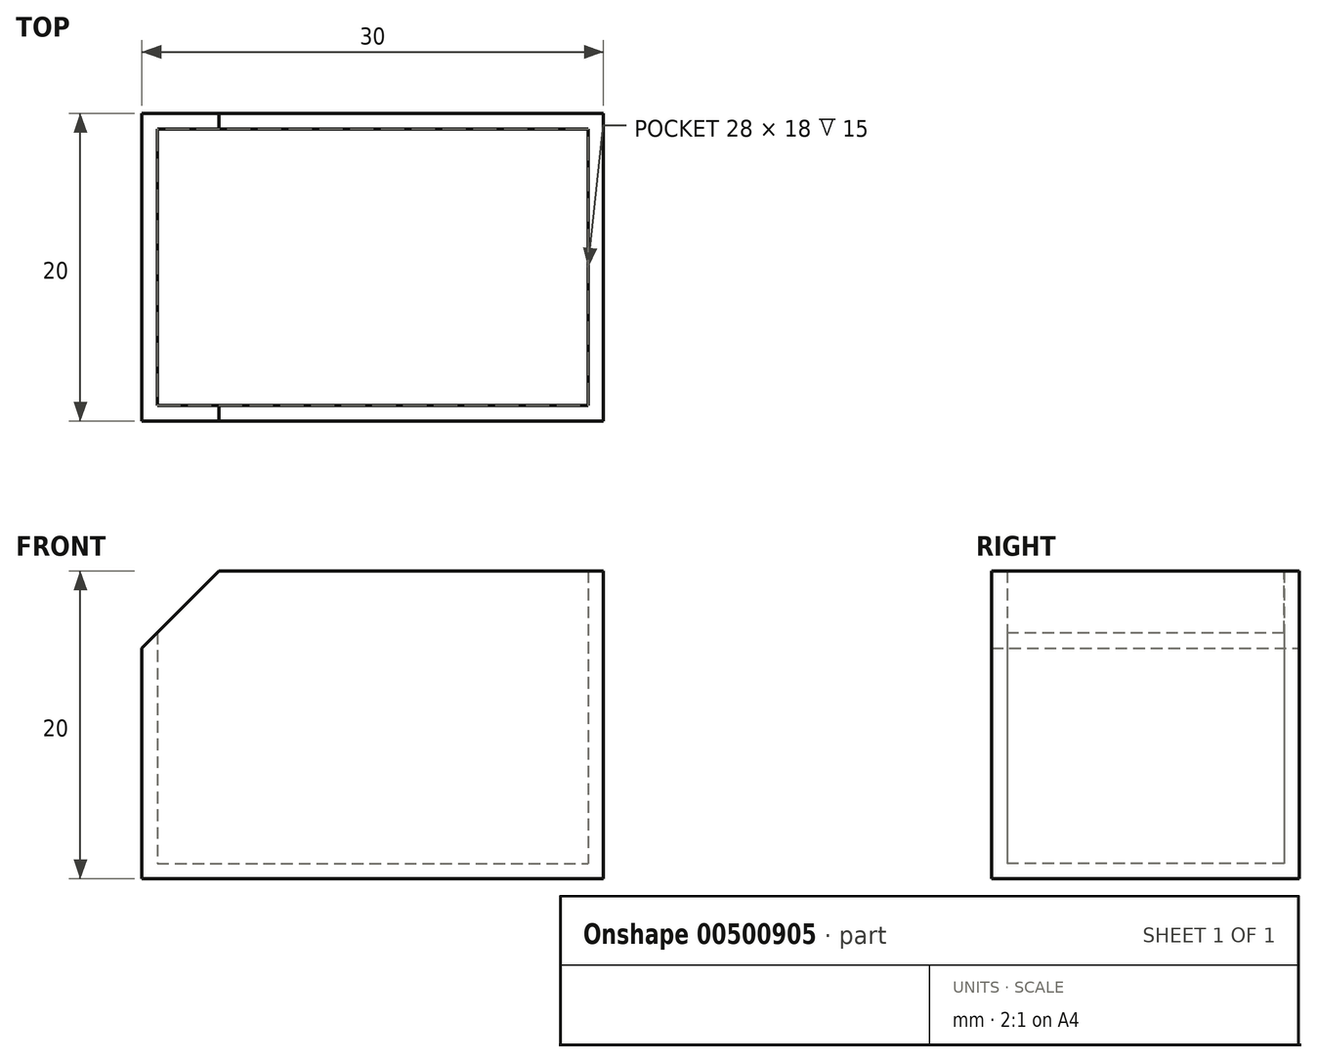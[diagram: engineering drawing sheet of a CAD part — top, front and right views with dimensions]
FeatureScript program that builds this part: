
annotation { "Feature Type Name" : "Feature", "Feature Type Description" : "" }
export const myFeature = defineFeature(function(context is Context, id is Id, definition is map)
    precondition{}
    {
        {
            var Q0;
            Q0=qCreatedBy(makeId("Front.planeOp"),FACE);
            var sketch = newSketch(context, id + "F0", { "sketchPlane" : qUnion([Q0])});
            skLineSegment(sketch, "E0.bottom", {"start": v(-15, 10) * mm, "end": v(15, 10) * mm});
            skLineSegment(sketch, "E0.top", {"start": v(-15, -10) * mm, "end": v(15, -10) * mm});
            skLineSegment(sketch, "E0.left", {"start": v(-15, 10) * mm, "end": v(-15, -10) * mm});
            skLineSegment(sketch, "E0.right", {"start": v(15, 10) * mm, "end": v(15, -10) * mm});
            skPoint(sketch, "E0.middle", {"position": v(0, 0) * mm});
            skSolve(sketch);
        }
        {
            var Q0;
            Q0 = qSketchRegion(id + "F0", true);
            extrude(context, id + "F1", {"entities" : qUnion([Q0]), "oppositeDirection" : true, "depth" : 10 * mm, "hasSecondDirection" : true, "secondDirectionOppositeDirection" : false, "secondDirectionDepth" : 10 * mm});
        }
        {
            var Q0;
            Q0=makeQuery(id+"F1.opExtrude","SWEPT_EDGE",EDGE,{"disambiguationData":[OSD([sQuery(id+"F0.wireOp",EDGE,"E0.bottom"),sQuery(id+"F0.wireOp",EDGE,"E0.left")])]});
            chamfer(context, id + "F2", {"entities" : qUnion([Q0]), "width" : 5 * mm, "tangentPropagation" : true});
        }
        {
            var Q0;
            Q0=makeQuery(id+"F1.opExtrude","SWEPT_FACE",FACE,{"disambiguationData":[OSD([sQuery(id+"F0.wireOp",EDGE,"E0.bottom")])]});
            var Q1;
            Q1=makeQuery(id+"F2.opChamfer","BLEND_FACE",FACE,{"disambiguationData":[OSD([sQuery(id+"F0.wireOp",EDGE,"E0.bottom"),sQuery(id+"F0.wireOp",EDGE,"E0.left")])]});
            shell(context, id + "F3", {"entities" : qUnion([Q0, Q1]), "thickness" : 1 * mm});
        }
    });
